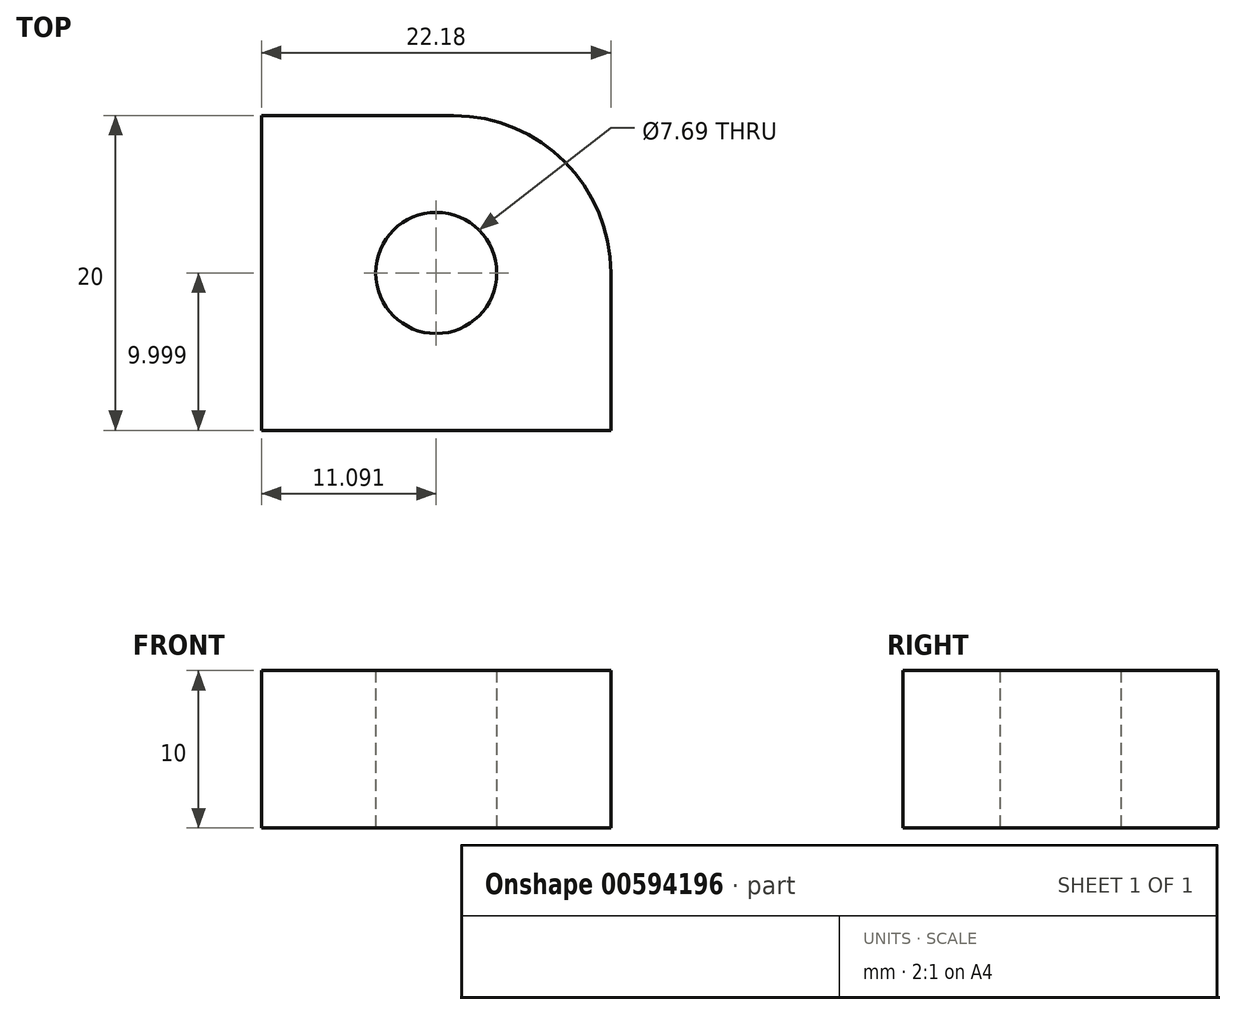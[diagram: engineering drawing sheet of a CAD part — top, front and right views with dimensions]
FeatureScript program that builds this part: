
annotation { "Feature Type Name" : "Feature", "Feature Type Description" : "" }
export const myFeature = defineFeature(function(context is Context, id is Id, definition is map)
    precondition{}
    {
        {
            var Q0;
            Q0=qCreatedBy(makeId("Top.planeOp"),FACE);
            var sketch = newSketch(context, id + "F0", { "sketchPlane" : qUnion([Q0])});
            skLineSegment(sketch, "E0.bottom", {"start": v(-15.62, 13.43) * mm, "end": v(-37.8, 13.43) * mm});
            skLineSegment(sketch, "E0.top", {"start": v(-25.62, 33.43) * mm, "end": v(-37.8, 33.43) * mm});
            skLineSegment(sketch, "E0.left", {"start": v(-15.62, 13.43) * mm, "end": v(-15.62, 23.43) * mm});
            skLineSegment(sketch, "E0.right", {"start": v(-37.8, 13.43) * mm, "end": v(-37.8, 33.43) * mm});
            skPoint(sketch, "E0.middle", {"position": v(-26.7, 23.43) * mm});
            skCircle(sketch, "E1", {"center": v(-26.7, 23.43) * mm, "radius": 3.85 * mm});
            skPoint(sketch, "E2.visualSharp", {"position": v(-15.62, 33.43) * mm});
            skArc(sketch, "E2.filletArc", {"start": v(-15.62, 23.43) * mm, "mid": v(-18.55, 30.5) * mm, "end": v(-25.62, 33.43) * mm});
            skSolve(sketch);
        }
        {
            var Q0;
            Q0=makeQuery(id+"F0.imprint","IMPRINT",FACE,{"disambiguationData":[TD([[makeQuery(id+"F0.imprint","IMPRINT",EDGE,{"derivedFrom":sQuery(id+"F0.wireOp",EDGE,"E0.bottom")}),-1.0]])]});
            extrude(context, id + "F1", {"entities" : qUnion([Q0]), "depth" : 10 * mm, "offsetDistance" : 25 * mm});
        }
    });
